# Revit family: TowelHolder-Long-Vitra-BaseSeries-A44109
name_source: partatom
category: Plumbing Fixtures
revit_build: Autodesk Revit 2017 (Build: 20160225_1515(x64)
units: mm (PartAtom-declared; Revit-internal decimal feet)

## family parameters
Cut with Voids When Loaded = No
Host = Face
OmniClass Number = 23.45.55.00
OmniClass Title = Sanitary Faucets, Wastes
Part Type = Normal
Room Calculation Point = No
Round Connector Dimension = Use Diameter
Shared = Yes

## types (1)
- TowelHolder-Long-Vitra-BaseSeries-A44109
    Article No. (default) = A44109
    BIMobject category = Sanitary - Bathroom Accessories
    Brand = VitrA
    CW Connection = No
    Coating Material = Chrome (Metal)
    Color = Chrome
    Default Elevation = 1050 mm
    Description = Base Towel Holder - Long
    Design country = Turkey
    HW Connection = No
    IFC Classification = Sanitary Terminal
    Main Material = Metal
    Manufacturer = Vitra
    Manufacturer name = Vitra
    Model = A44109
    Mounting type = Wall Mounted
    NBS Referans Code = 35-75-90
    NBS Referans Description = Towel Rails
    Nominal Depth (mm) = 53 mm  [stored 0.173885 ft]
    Nominal Height (mm) = 50 mm
    Nominal Width (mm) = 516 mm  [stored 1.69291 ft]
    OmniClass Code = 23-31 25 25
    OmniClass Description = Towel Bars
    Product SKU = A44109
    Product Type = Built In Towel Holder Long
    Product certification = https://www.vitraglobal.com
    Product family = Base Series
    Product group = Towel Holder Long
    Product url = https://vitraglobal.com
    Technical description = https://vitraglobal.com
    UNSPSC Description = Furniture and Furnishings
    URL = https://vitraglobal.com
    Uniclass 1.4 Code = L8245
    Uniclass 1.4 Description = Towel rails
    Uniclass 2.0 Code = PR-35-75-90
    Uniclass 2.0 Description = Towel Rails
    Uniclass 2015 Code = Pr_40_20_76_90
    Uniclass 2015 Name = Towel rails
    Uniformat II Code = E2010
    Uniformat II Description = FURNISHINGS
    Vent Connection = No
    Warranty Period (Year) = 5 years
    Waste Connection = No
    Weight Net (kg) = 2
    Youtube = https://www.youtube.com

note: [stored X ft] marks values corroborated as IEEE doubles in the binary element streams (Revit-internal decimal feet)

## geometry (parser evidence)
native form markers: Sweep x3
no freeform markers — native parametric forms only
